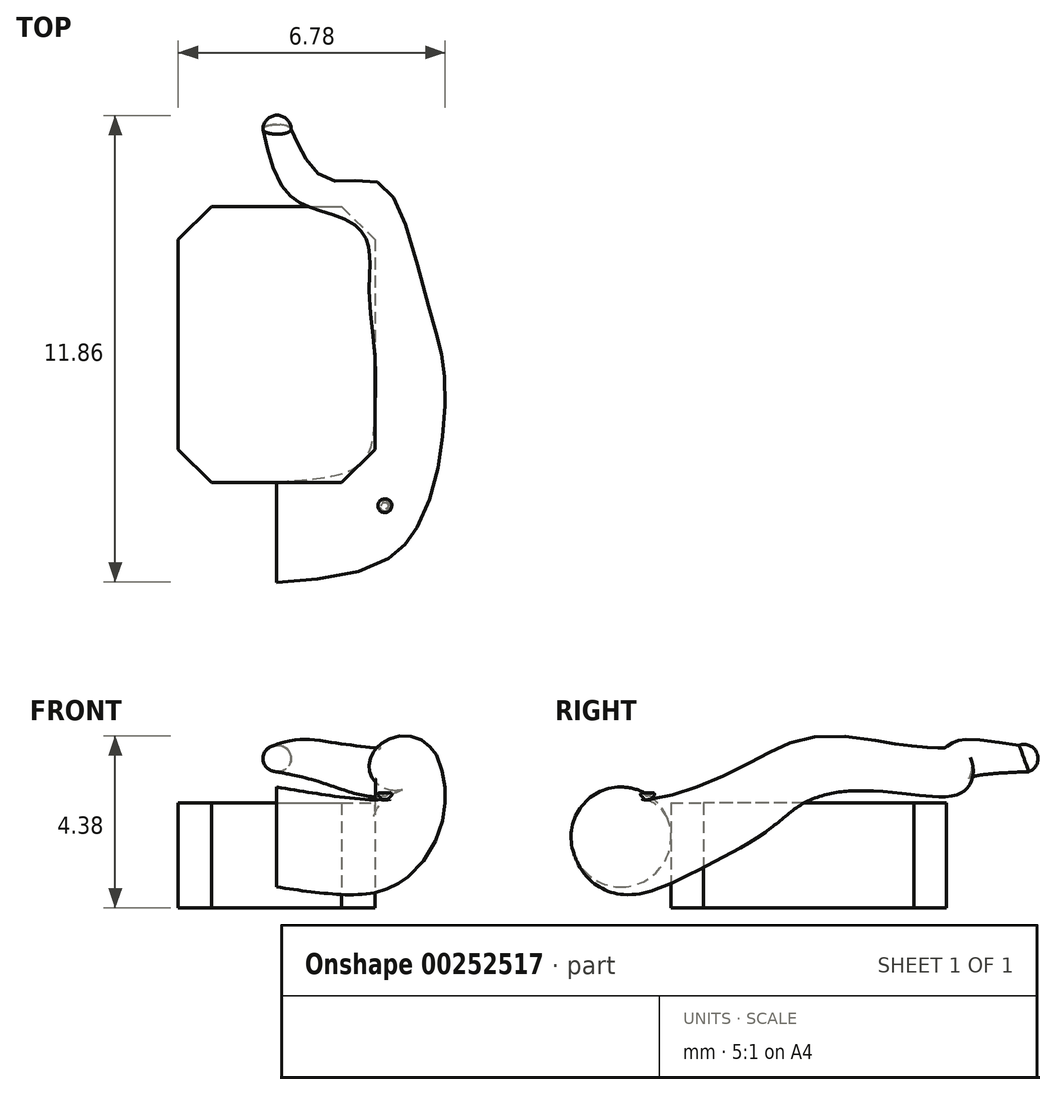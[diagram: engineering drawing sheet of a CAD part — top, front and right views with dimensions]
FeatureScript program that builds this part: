
annotation { "Feature Type Name" : "Feature", "Feature Type Description" : "" }
export const myFeature = defineFeature(function(context is Context, id is Id, definition is map)
    precondition{}
    {
        {
            var Q0;
            Q0=qCreatedBy(makeId("Top.planeOp"),FACE);
            var sketch = newSketch(context, id + "F0", { "sketchPlane" : qUnion([Q0])});
            skLineSegment(sketch, "E0.bottom", {"start": v(-6.75, -3.03) * mm, "end": v(-3.46, -3.03) * mm});
            skLineSegment(sketch, "E0.top", {"start": v(-6.75, -10.03) * mm, "end": v(-3.46, -10.03) * mm});
            skLineSegment(sketch, "E0.left", {"start": v(-7.6, -3.86) * mm, "end": v(-7.6, -9.2) * mm});
            skLineSegment(sketch, "E0.right", {"start": v(-2.6, -3.86) * mm, "end": v(-2.6, -9.2) * mm});
            skLineSegment(sketch, "E1", {"start": v(-5.1, -3.03) * mm, "end": v(-5.1, -13.2) * mm, "construction": true});
            skLineSegment(sketch, "E2", {"start": v(-7.6, -6.53) * mm, "end": v(0, -6.53) * mm, "construction": true});
            skLineSegment(sketch, "E3", {"start": v(-6.75, -3.03) * mm, "end": v(-7.6, -3.86) * mm});
            skLineSegment(sketch, "E4.MirrorCS", {"start": v(-3.46, -3.03) * mm, "end": v(-2.6, -3.86) * mm});
            skLineSegment(sketch, "E5.MirrorCS", {"start": v(-6.75, -10.03) * mm, "end": v(-7.6, -9.2) * mm});
            skLineSegment(sketch, "E6.MirrorCS", {"start": v(-3.46, -10.03) * mm, "end": v(-2.6, -9.2) * mm});
            skSolve(sketch);
        }
        {
            var Q0;
            Q0=makeQuery(id+"F0.imprint","IMPRINT",FACE,{"disambiguationData":[TD([[makeQuery(id+"F0.imprint","IMPRINT",EDGE,{"derivedFrom":sQuery(id+"F0.wireOp",EDGE,"E0.bottom")}),-1.0]])]});
            extrude(context, id + "F1", {"entities" : qUnion([Q0]), "depth" : 2.67 * mm});
        }
        {
            var Q0;
            Q0=makeQuery(id+"F1.opExtrude","CAP_EDGE",EDGE,{"disambiguationData":[OSD([sQuery(id+"F0.wireOp",EDGE,"E0.top")])],"isStart":false});
            cPoint(context, id + "F2", {"entities" : qUnion([Q0]), "parameter" : 0.5});
        }
        {
            var Q0;
            Q0=makeQuery(id+"F1.opExtrude","CAP_EDGE",EDGE,{"disambiguationData":[OSD([sQuery(id+"F0.wireOp",EDGE,"E0.top")])],"isStart":true});
            cPoint(context, id + "F3", {"entities" : qUnion([Q0]), "parameter" : 0.5});
        }
        {
            var Q0;
            Q0=makeQuery(id+"F1.opExtrude","CAP_EDGE",EDGE,{"disambiguationData":[OSD([sQuery(id+"F0.wireOp",EDGE,"E0.bottom")])],"isStart":false});
            cPoint(context, id + "F4", {"entities" : qUnion([Q0]), "parameter" : 0.5});
        }
        {
            var Q0;
            Q0 = qCreatedBy(id + "F2" ,VERTEX);
            var Q1;
            Q1 = qCreatedBy(id + "F3" ,VERTEX);
            var Q2;
            Q2 = qCreatedBy(id + "F4" ,VERTEX);
            cPlane(context, id + "F5", {"entities" : qUnion([Q0, Q1, Q2]), "cplaneType" : CPlaneType.THREE_POINT, "offset" : 25.4 * mm, "width" : 152.4 * mm, "height" : 152.4 * mm});
        }
        {
            var Q0;
            Q0=qCreatedBy(id+"F5.planeOp",FACE);
            var sketch = newSketch(context, id + "F6", { "sketchPlane" : qUnion([Q0])});
            skLineSegment(sketch, "E7", {"start": v(10.03, 2.67) * mm, "end": v(10.03, 0) * mm});
            skArc(sketch, "E8", {"start": v(11.32, 3.08) * mm, "mid": v(10.03, 1.8) * mm, "end": v(11.34, 0.54) * mm});
            skArc(sketch, "E9", {"start": v(11.34, 0.54) * mm, "mid": v(12.57, 1.82) * mm, "end": v(11.32, 3.08) * mm});
            skSolve(sketch);
        }
        {
            var Q0;
            Q0=makeQuery(id+"F1.opExtrude","CAP_EDGE",EDGE,{"disambiguationData":[OSD([sQuery(id+"F0.wireOp",EDGE,"E6.MirrorCS")])],"isStart":false});
            cPoint(context, id + "F7", {"entities" : qUnion([Q0]), "parameter" : 0.5});
        }
        {
            var Q0;
            Q0=makeQuery(id+"F1.opExtrude","CAP_EDGE",EDGE,{"disambiguationData":[OSD([sQuery(id+"F0.wireOp",EDGE,"E6.MirrorCS")])],"isStart":true});
            cPoint(context, id + "F8", {"entities" : qUnion([Q0]), "parameter" : 0.5});
        }
        {
            var Q0;
            Q0=makeQuery(id+"F1.opExtrude","CAP_EDGE",EDGE,{"disambiguationData":[OSD([sQuery(id+"F0.wireOp",EDGE,"E3")])],"isStart":false});
            cPoint(context, id + "F9", {"entities" : qUnion([Q0]), "parameter" : 0.5});
        }
        {
            var Q0;
            Q0 = qCreatedBy(id + "F7" ,VERTEX);
            var Q1;
            Q1 = qCreatedBy(id + "F8" ,VERTEX);
            var Q2;
            Q2 = qCreatedBy(id + "F9" ,VERTEX);
            cPlane(context, id + "F10", {"entities" : qUnion([Q0, Q1, Q2]), "cplaneType" : CPlaneType.THREE_POINT, "offset" : 25.4 * mm, "width" : 152.4 * mm, "height" : 152.4 * mm});
        }
        {
            var Q0;
            Q0=qCreatedBy(id+"F10.planeOp",FACE);
            var sketch = newSketch(context, id + "F11", { "sketchPlane" : qUnion([Q0])});
            skLineSegment(sketch, "E10", {"start": v(6.29, 2.67) * mm, "end": v(6.29, 0) * mm});
            skArc(sketch, "E11", {"start": v(7.47, 2.76) * mm, "mid": v(6.3, 1.58) * mm, "end": v(7.54, 0.48) * mm});
            skArc(sketch, "E12", {"start": v(7.54, 0.48) * mm, "mid": v(8.57, 1.65) * mm, "end": v(7.47, 2.76) * mm});
            skSolve(sketch);
        }
        {
            var Q0;
            Q0=makeQuery(id+"F1.opExtrude","CAP_EDGE",EDGE,{"disambiguationData":[OSD([sQuery(id+"F0.wireOp",EDGE,"E0.top")])],"isStart":false});
            cPlane(context, id + "F12", {"entities" : qUnion([Q0]), "cplaneType" : CPlaneType.LINE_ANGLE, "offset" : 25.4 * mm, "angle" : 20 * degree, "width" : 152.4 * mm, "height" : 152.4 * mm});
        }
        {
            var Q0;
            Q0=qCreatedBy(id+"F12.planeOp",FACE);
            cPlane(context, id + "F13", {"entities" : qUnion([Q0]), "cplaneType" : CPlaneType.OFFSET, "offset" : 1.83 * mm, "width" : 152.4 * mm, "height" : 152.4 * mm});
        }
        {
            var Q0;
            Q0=qCreatedBy(id+"F13.planeOp",FACE);
            var sketch = newSketch(context, id + "F14", { "sketchPlane" : qUnion([Q0])});
            skLineSegment(sketch, "E13", {"start": v(2.6, 5.27) * mm, "end": v(2.6, 2.43) * mm});
            skArc(sketch, "E14", {"start": v(1.73, 6.16) * mm, "mid": v(0.83, 5.29) * mm, "end": v(1.7, 4.38) * mm});
            skArc(sketch, "E15", {"start": v(1.7, 4.38) * mm, "mid": v(2.6, 5.25) * mm, "end": v(1.73, 6.16) * mm});
            skSolve(sketch);
        }
        {
            var Q0;
            Q0=makeQuery(id+"F1.opExtrude","CAP_EDGE",EDGE,{"disambiguationData":[OSD([sQuery(id+"F0.wireOp",EDGE,"E0.bottom")])],"isStart":false});
            cPlane(context, id + "F15", {"entities" : qUnion([Q0]), "cplaneType" : CPlaneType.LINE_ANGLE, "offset" : 25.4 * mm, "angle" : 22.6 * degree, "oppositeDirection" : true, "width" : 152.4 * mm, "height" : 152.4 * mm});
        }
        {
            var Q0;
            Q0=qCreatedBy(id+"F15.planeOp",FACE);
            cPlane(context, id + "F16", {"entities" : qUnion([Q0]), "cplaneType" : CPlaneType.OFFSET, "offset" : 2.24 * mm, "oppositeDirection" : true, "width" : 152.4 * mm, "height" : 152.4 * mm});
        }
        {
            var Q0;
            Q0=qCreatedBy(id+"F16.planeOp",FACE);
            var sketch = newSketch(context, id + "F17", { "sketchPlane" : qUnion([Q0])});
            skArc(sketch, "E16", {"start": v(2.04, 2.08) * mm, "mid": v(1.38, 1.4) * mm, "end": v(2.04, 0.7) * mm});
            skArc(sketch, "E17", {"start": v(2.04, 0.7) * mm, "mid": v(2.75, 1.4) * mm, "end": v(2.04, 2.08) * mm});
            skSolve(sketch);
        }
        {
            var Q0;
            Q0=makeQuery(id+"F1.opExtrude","CAP_EDGE",EDGE,{"disambiguationData":[OSD([sQuery(id+"F0.wireOp",EDGE,"E4.MirrorCS")])],"isStart":false});
            cPoint(context, id + "F18", {"entities" : qUnion([Q0]), "parameter" : 0.5});
        }
        {
            var Q0;
            Q0=makeQuery(id+"F1.opExtrude","CAP_EDGE",EDGE,{"disambiguationData":[OSD([sQuery(id+"F0.wireOp",EDGE,"E4.MirrorCS")])],"isStart":true});
            cPoint(context, id + "F19", {"entities" : qUnion([Q0]), "parameter" : 0.5});
        }
        {
            var Q0;
            Q0=makeQuery(id+"F1.opExtrude","CAP_EDGE",EDGE,{"disambiguationData":[OSD([sQuery(id+"F0.wireOp",EDGE,"E5.MirrorCS")])],"isStart":false});
            cPoint(context, id + "F20", {"entities" : qUnion([Q0]), "parameter" : 0.5});
        }
        {
            var Q0;
            Q0 = qCreatedBy(id + "F18" ,VERTEX);
            var Q1;
            Q1 = qCreatedBy(id + "F19" ,VERTEX);
            var Q2;
            Q2 = qCreatedBy(id + "F20" ,VERTEX);
            cPlane(context, id + "F21", {"entities" : qUnion([Q0, Q1, Q2]), "cplaneType" : CPlaneType.THREE_POINT, "offset" : 25.4 * mm, "width" : 152.4 * mm, "height" : 152.4 * mm});
        }
        {
            var Q0;
            Q0=qCreatedBy(id+"F21.planeOp",FACE);
            var sketch = newSketch(context, id + "F22", { "sketchPlane" : qUnion([Q0])});
            skArc(sketch, "E18", {"start": v(-3.73, 4) * mm, "mid": v(-4.56, 3.76) * mm, "end": v(-4.34, 2.92) * mm});
            skArc(sketch, "E19", {"start": v(-4.34, 2.92) * mm, "mid": v(-3.48, 3.15) * mm, "end": v(-3.73, 4) * mm});
            skSolve(sketch);
        }
        {
            var Q0;
            Q0=qCreatedBy(id+"F21.planeOp",FACE);
            cPlane(context, id + "F23", {"entities" : qUnion([Q0]), "cplaneType" : CPlaneType.OFFSET, "offset" : 1.52 * mm, "oppositeDirection" : true, "width" : 152.4 * mm, "height" : 152.4 * mm});
        }
        {
            var Q0;
            Q0=qCreatedBy(id+"F13.planeOp",FACE);
            cPlane(context, id + "F24", {"entities" : qUnion([Q0]), "cplaneType" : CPlaneType.OFFSET, "offset" : 6.98 * mm, "width" : 152.4 * mm, "height" : 152.4 * mm});
        }
        {
            var Q0;
            Q0=qCreatedBy(id+"F24.planeOp",FACE);
            var sketch = newSketch(context, id + "F25", { "sketchPlane" : qUnion([Q0])});
            skCircle(sketch, "E20", {"center": v(5.1, 3.94) * mm, "radius": 0.36 * mm});
            skLineSegment(sketch, "E21", {"start": v(4.88, 4.22) * mm, "end": v(5.3, 3.65) * mm});
            skSolve(sketch);
        }
        {
            var Q0;
            {var subQ0=sQuery(id+"F25.wireOp",EDGE,"E21");Q0=makeQuery(id+"F25.imprint","IMPRINT",FACE,{"disambiguationData":[TD([[makeQuery(id+"F25.imprint","IMPRINT",EDGE,{"derivedFrom":subQ0}),1.0]])]});}
            var Q1;
            Q1=sQuery(id+"F25.wireOp",EDGE,"E21");
            revolve(context, id + "F26", {"entities" : qUnion([Q0]), "axis" : qUnion([Q1]), "revolveType" : RevolveType.ONE_DIRECTION, "angle" : 180 * degree});
        }
        {
            var Q0;
            Q0=qCreatedBy(id+"F16.planeOp",FACE);
            var Q1;
            Q1=qCreatedBy(id+"F13.planeOp",FACE);
            cPlane(context, id + "F27", {"entities" : qUnion([Q0, Q1]), "cplaneType" : CPlaneType.MID_PLANE, "offset" : 25.4 * mm, "flipAlignment" : true, "width" : 152.4 * mm, "height" : 152.4 * mm});
        }
        {
            var Q0;
            Q0=qCreatedBy(id+"F27.planeOp",FACE);
            var sketch = newSketch(context, id + "F28", { "sketchPlane" : qUnion([Q0])});
            skArc(sketch, "E22", {"start": v(1.75, 4.13) * mm, "mid": v(0.92, 3.26) * mm, "end": v(1.8, 2.44) * mm});
            skArc(sketch, "E23", {"start": v(1.8, 2.44) * mm, "mid": v(2.6, 3.3) * mm, "end": v(1.75, 4.13) * mm});
            skSolve(sketch);
        }
        {
            var Q0;
            {var subQ0=sQuery(id+"F25.wireOp",EDGE,"E21");Q0=makeQuery(id+"F25.imprint","IMPRINT",FACE,{"disambiguationData":[TD([[makeQuery(id+"F25.imprint","IMPRINT",EDGE,{"derivedFrom":subQ0}),-1.0]])]});}
            var sketch = newSketch(context, id + "F29", { "sketchPlane" : qUnion([Q0])});
            skArc(sketch, "E24", {"start": v(5.1, 4.3) * mm, "mid": v(4.73, 3.94) * mm, "end": v(5.1, 3.58) * mm});
            skArc(sketch, "E25", {"start": v(5.1, 3.58) * mm, "mid": v(5.45, 3.94) * mm, "end": v(5.1, 4.3) * mm});
            skSolve(sketch);
        }
        {
            var Q0;
            Q0=qCreatedBy(id+"F21.planeOp",FACE);
            var Q1;
            Q1=qCreatedBy(id+"F24.planeOp",FACE);
            cPlane(context, id + "F30", {"entities" : qUnion([Q0, Q1]), "cplaneType" : CPlaneType.MID_PLANE, "offset" : 25.4 * mm, "width" : 152.4 * mm, "height" : 152.4 * mm});
        }
        {
            var Q0;
            Q0=qCreatedBy(id+"F30.planeOp",FACE);
            var sketch = newSketch(context, id + "F31", { "sketchPlane" : qUnion([Q0])});
            skArc(sketch, "E26", {"start": v(-4.4, 4.75) * mm, "mid": v(-5, 4.36) * mm, "end": v(-4.6, 3.77) * mm});
            skArc(sketch, "E27", {"start": v(-4.6, 3.77) * mm, "mid": v(-4.01, 4.16) * mm, "end": v(-4.4, 4.75) * mm});
            skSolve(sketch);
        }
        {
            var Q1;
            {var subQ0=sQuery(id+"F6.wireOp",EDGE,"E9");Q1=makeQuery(id+"F6.imprint","IMPRINT",FACE,{"disambiguationData":[TD([[makeQuery(id+"F6.imprint","IMPRINT",EDGE,{"derivedFrom":subQ0}),1.0]])]});}
            var Q2;
            {var subQ0=sQuery(id+"F11.wireOp",EDGE,"E12");Q2=makeQuery(id+"F11.imprint","IMPRINT",FACE,{"disambiguationData":[TD([[makeQuery(id+"F11.imprint","IMPRINT",EDGE,{"derivedFrom":subQ0}),1.0]])]});}
            var Q3;
            {var subQ0=sQuery(id+"F14.wireOp",EDGE,"E14");Q3=makeQuery(id+"F14.imprint","IMPRINT",FACE,{"disambiguationData":[TD([[makeQuery(id+"F14.imprint","IMPRINT",EDGE,{"derivedFrom":subQ0}),1.0]])]});}
            var Q4;
            Q4=makeQuery(id+"F28.imprint","IMPRINT",FACE,{"disambiguationData":[TD([[makeQuery(id+"F28.imprint","IMPRINT",EDGE,{"derivedFrom":sQuery(id+"F28.wireOp",EDGE,"E22")}),1.0]])]});
            var Q5;
            Q5=makeQuery(id+"F17.imprint","IMPRINT",FACE,{"disambiguationData":[TD([[makeQuery(id+"F17.imprint","IMPRINT",EDGE,{"derivedFrom":sQuery(id+"F17.wireOp",EDGE,"E16")}),1.0]])]});
            var Q6;
            Q6=makeQuery(id+"F22.imprint","IMPRINT",FACE,{"disambiguationData":[TD([[makeQuery(id+"F22.imprint","IMPRINT",EDGE,{"derivedFrom":sQuery(id+"F22.wireOp",EDGE,"E18")}),1.0]])]});
            var Q7;
            Q7=makeQuery(id+"F31.imprint","IMPRINT",FACE,{"disambiguationData":[TD([[makeQuery(id+"F31.imprint","IMPRINT",EDGE,{"derivedFrom":sQuery(id+"F31.wireOp",EDGE,"E26")}),1.0]])]});
            var Q8;
            Q8 = qSketchRegion(id + "F29", true);
            var Q9;
            Q9=sQuery(id+"F6.wireOp",VERTEX,"E9.start");
            var Q10;
            Q10=sQuery(id+"F11.wireOp",VERTEX,"E12.start");
            var Q11;
            Q11=sQuery(id+"F14.wireOp",VERTEX,"E15.start");
            var Q12;
            Q12=sQuery(id+"F28.wireOp",VERTEX,"E22.end");
            var Q13;
            Q13=sQuery(id+"F17.wireOp",VERTEX,"E17.start");
            var Q14;
            Q14=sQuery(id+"F22.wireOp",VERTEX,"E19.start");
            var Q15;
            Q15=sQuery(id+"F31.wireOp",VERTEX,"E27.start");
            var Q16;
            Q16=sQuery(id+"F29.wireOp",VERTEX,"E24.end");
            loft(context, id + "F32", {"sheetProfilesArray" : [{ "sheetProfileEntities" : qUnion([Q1]) }, { "sheetProfileEntities" : qUnion([Q2]) }, { "sheetProfileEntities" : qUnion([Q3]) }, { "sheetProfileEntities" : qUnion([Q4]) }, { "sheetProfileEntities" : qUnion([Q5]) }, { "sheetProfileEntities" : qUnion([Q6]) }, { "sheetProfileEntities" : qUnion([Q7]) }, { "sheetProfileEntities" : qUnion([Q8]) }], "matchConnections" : true, "connections" : [{ "connectionEntities" : qUnion([Q9, Q10, Q11, Q12, Q13, Q14, Q15, Q16]), "connectionEdgeQueries" : qUnion([]), "connectionEdgeParameters" : [] }]});
        }
        {
            var Q0;
            Q0=qCreatedBy(id+"F10.planeOp",FACE);
            var sketch = newSketch(context, id + "F33", { "sketchPlane" : qUnion([Q0])});
            skFitSpline(sketch, "E28", {"points": [v(7.54, 0.48) * mm, v(7.7, 0.5) * mm, v(7.84, 0.54) * mm, v(8.1, 0.68) * mm, v(8.22, 0.77) * mm, v(8.4, 1) * mm, v(8.47, 1.12) * mm, v(8.56, 1.4) * mm, v(8.58, 1.54) * mm, v(8.57, 1.82) * mm, v(8.53, 1.96) * mm, v(8.42, 2.21) * mm, v(8.34, 2.33) * mm, v(8.13, 2.53) * mm, v(8.02, 2.6) * mm, v(7.75, 2.72) * mm, v(7.61, 2.75) * mm, v(7.36, 2.76) * mm, v(7.26, 2.75) * mm, v(7.05, 2.7) * mm, v(6.95, 2.66) * mm, v(6.77, 2.55) * mm, v(6.69, 2.49) * mm, v(6.54, 2.34) * mm, v(6.48, 2.26) * mm, v(6.38, 2.08) * mm, v(6.34, 1.98) * mm, v(6.3, 1.78) * mm, v(6.29, 1.68) * mm, v(6.3, 1.48) * mm, v(6.3, 1.39) * mm, v(6.37, 1.19) * mm, v(6.41, 1.09) * mm, v(6.53, 0.91) * mm, v(6.6, 0.83) * mm, v(6.75, 0.7) * mm, v(6.84, 0.63) * mm, v(7.03, 0.54) * mm, v(7.13, 0.5) * mm, v(7.34, 0.47) * mm, v(7.45, 0.47) * mm, v(7.54, 0.48) * mm]});
            skLineSegment(sketch, "E29", {"start": v(7.5, 2.65) * mm, "end": v(7.5, 2.85) * mm});
            skArc(sketch, "E30", {"start": v(7.66, 2.84) * mm, "mid": v(7.67, 2.92) * mm, "end": v(7.6, 2.9) * mm});
            skArc(sketch, "E31", {"start": v(7.5, 2.85) * mm, "mid": v(7.56, 2.87) * mm, "end": v(7.6, 2.9) * mm});
            skLineSegment(sketch, "E32.bottom", {"start": v(7.5, 2.65) * mm, "end": v(7.59, 2.65) * mm});
            skLineSegment(sketch, "E32.top", {"start": v(7.5, 2.73) * mm, "end": v(7.59, 2.73) * mm});
            skLineSegment(sketch, "E32.left", {"start": v(7.5, 2.65) * mm, "end": v(7.5, 2.73) * mm});
            skArc(sketch, "E33", {"start": v(7.66, 2.84) * mm, "mid": v(7.6, 2.8) * mm, "end": v(7.59, 2.73) * mm});
            skLineSegment(sketch, "E34", {"start": v(7.59, 2.73) * mm, "end": v(7.59, 2.65) * mm});
            skSolve(sketch);
        }
        {
            var Q0;
            {var subQ1=sQuery(id+"F33.wireOp",EDGE,"E30");Q0=makeQuery(id+"F33.imprint","IMPRINT",FACE,{"disambiguationData":[TD([[makeQuery(id+"F33.imprint","IMPRINT",EDGE,{"derivedFrom":subQ1}),1.0]])]});}
            var Q1;
            Q1=sQuery(id+"F33.wireOp",EDGE,"E29");
            revolve(context, id + "F34", {"entities" : qUnion([Q0]), "axis" : qUnion([Q1]), "revolveType" : RevolveType.FULL});
        }
        {
            var Q0;
            Q0=makeQuery(id+"F33.imprint","IMPRINT",FACE,{"disambiguationData":[TD([[makeQuery(id+"F33.imprint","IMPRINT",EDGE,{"derivedFrom":sQuery(id+"F33.wireOp",EDGE,"E32.bottom")}),1.0]])]});
            var Q1;
            Q1=sQuery(id+"F33.wireOp",EDGE,"E32.left");
            revolve(context, id + "F35", {"operationType" : NewBodyOperationType.ADD, "entities" : qUnion([Q0]), "axis" : qUnion([Q1]), "revolveType" : RevolveType.FULL});
        }
    });
